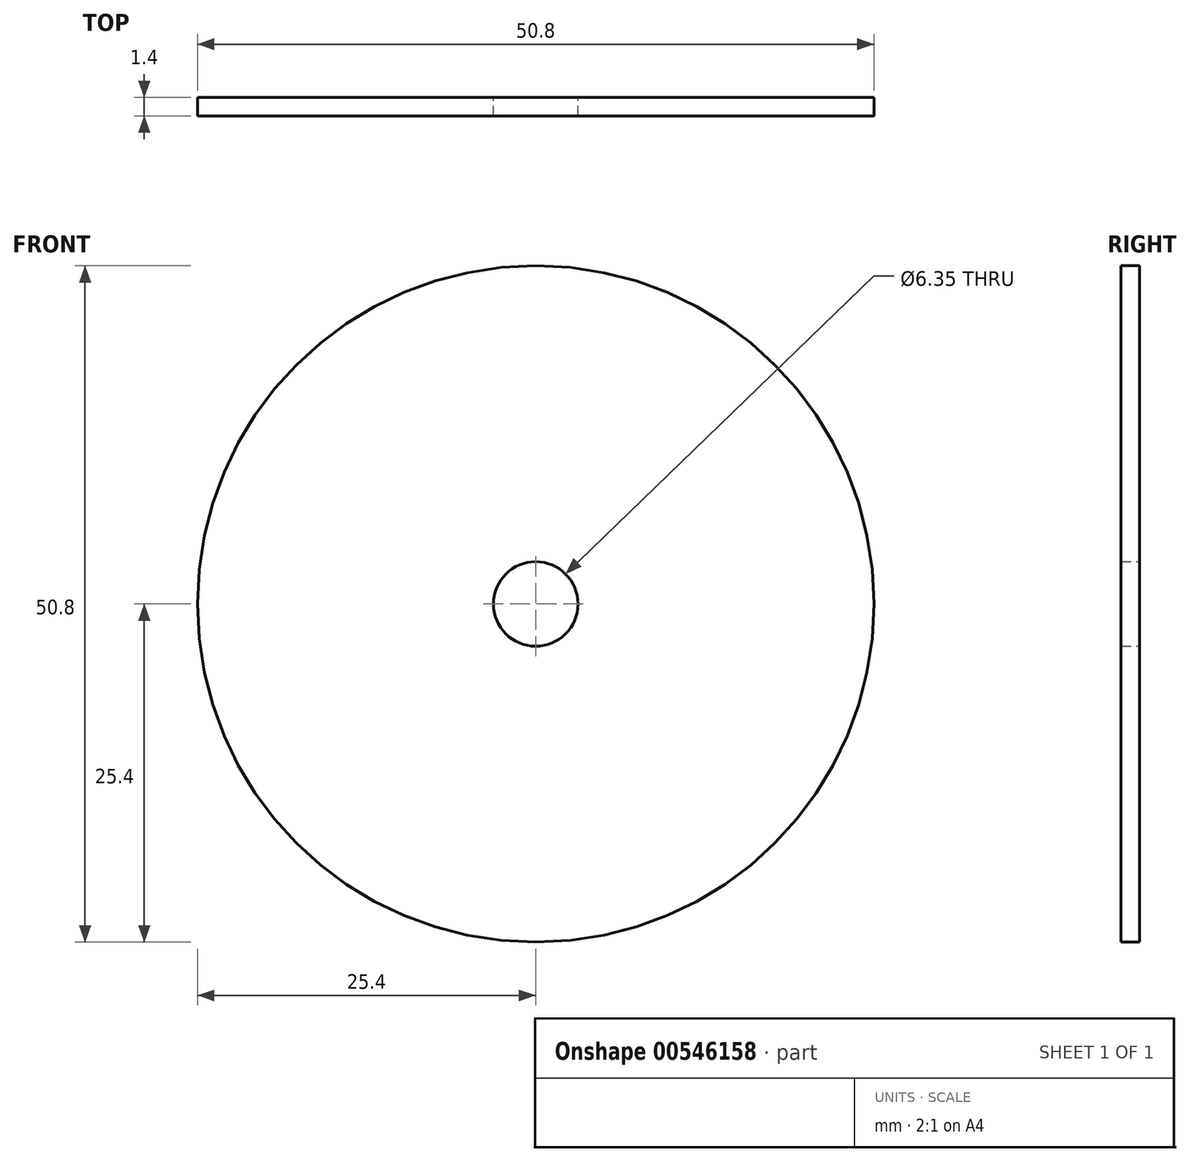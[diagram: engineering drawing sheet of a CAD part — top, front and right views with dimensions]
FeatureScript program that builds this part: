
annotation { "Feature Type Name" : "Feature", "Feature Type Description" : "" }
export const myFeature = defineFeature(function(context is Context, id is Id, definition is map)
    precondition{}
    {
        {
            var Q0;
            Q0=qCreatedBy(makeId("Front.planeOp"),FACE);
            var sketch = newSketch(context, id + "F0", { "sketchPlane" : qUnion([Q0])});
            skCircle(sketch, "E0", {"center": v(0, 0) * mm, "radius": 25.4 * mm});
            skCircle(sketch, "E1", {"center": v(0, 0) * mm, "radius": 3.18 * mm});
            skSolve(sketch);
        }
        {
            var Q0;
            Q0=qCreatedBy(makeId("Front.planeOp"),FACE);
            var sketch = newSketch(context, id + "F1", { "sketchPlane" : qUnion([Q0])});
            skSolve(sketch);
        }
        {
            var Q0;
            Q0 = qSketchRegion(id + "F1", true);
            var Q1;
            Q1=makeQuery(id+"F0.imprint","IMPRINT",FACE,{"disambiguationData":[TD([[makeQuery(id+"F0.imprint","IMPRINT",EDGE,{"derivedFrom":sQuery(id+"F0.wireOp",EDGE,"E0")}),1.0]])]});
            extrude(context, id + "F2", {"entities" : qUnion([Q0, Q1]), "depth" : 1.4 * mm, "offsetDistance" : 25.4 * mm});
        }
    });
